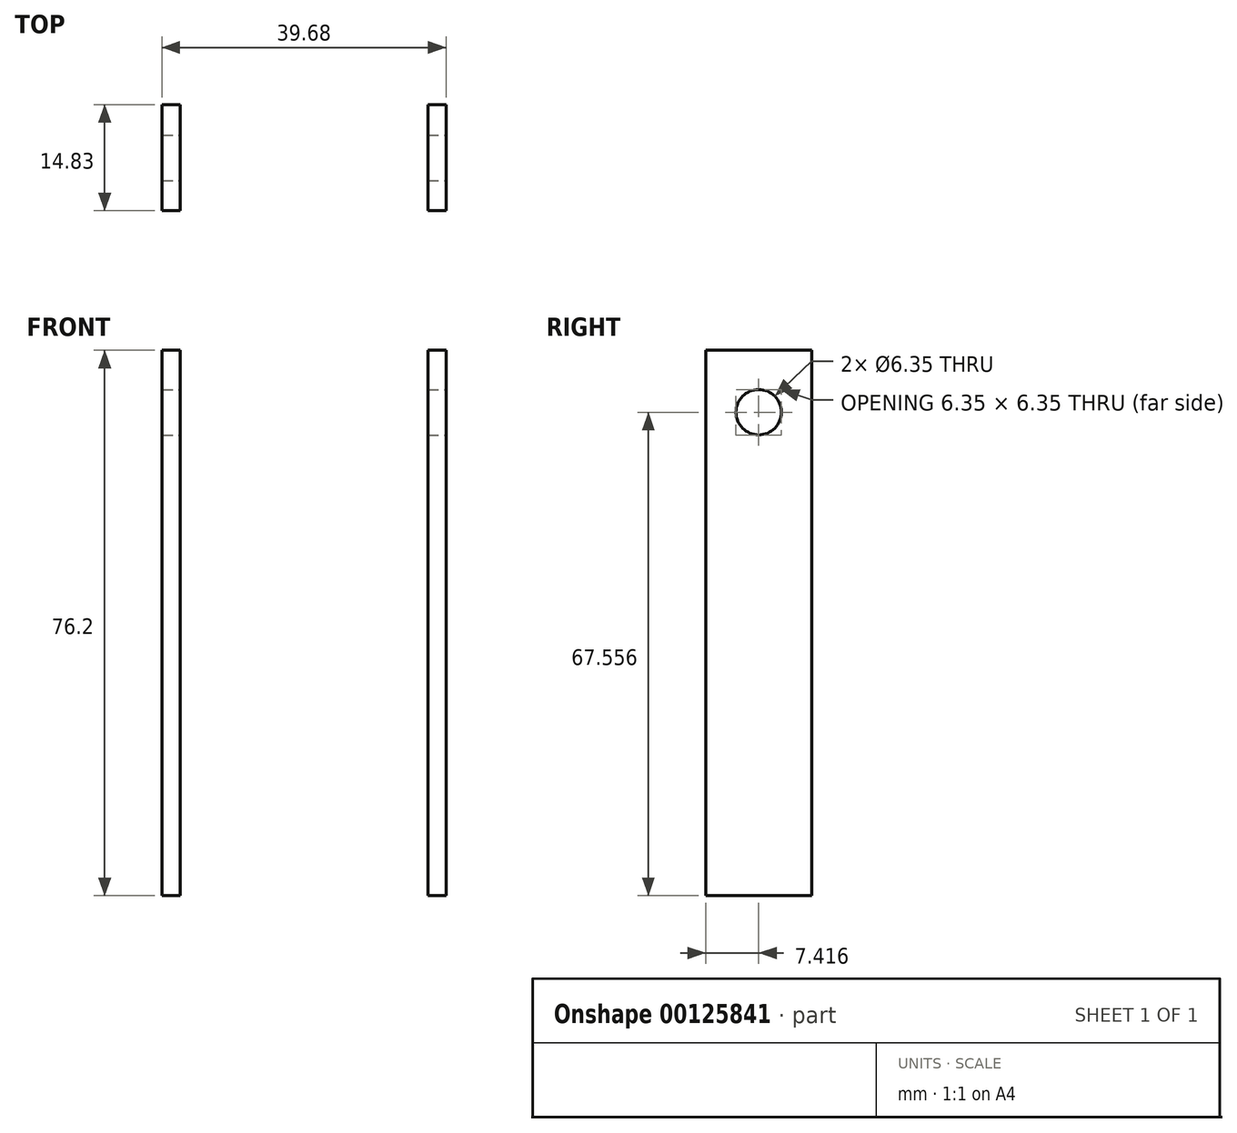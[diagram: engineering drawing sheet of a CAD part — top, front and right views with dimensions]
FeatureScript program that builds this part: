
annotation { "Feature Type Name" : "Feature", "Feature Type Description" : "" }
export const myFeature = defineFeature(function(context is Context, id is Id, definition is map)
    precondition{}
    {
        {
            var Q0;
            Q0=qCreatedBy(makeId("Front.planeOp"),FACE);
            var sketch = newSketch(context, id + "F0", { "sketchPlane" : qUnion([Q0])});
            skLineSegment(sketch, "E0", {"start": v(-12.93, -36.38) * mm, "end": v(-12.93, 39.82) * mm});
            skLineSegment(sketch, "E1", {"start": v(-12.93, 39.82) * mm, "end": v(-10.4, 39.82) * mm});
            skLineSegment(sketch, "E2", {"start": v(-10.4, 39.82) * mm, "end": v(-10.4, -36.38) * mm});
            skLineSegment(sketch, "E3", {"start": v(-10.4, -36.38) * mm, "end": v(-12.93, -36.38) * mm});
            skLineSegment(sketch, "E4", {"start": v(24.21, -36.38) * mm, "end": v(24.21, 39.82) * mm});
            skLineSegment(sketch, "E5", {"start": v(24.21, 39.82) * mm, "end": v(26.75, 39.82) * mm});
            skLineSegment(sketch, "E6", {"start": v(26.75, 39.82) * mm, "end": v(26.75, -36.38) * mm});
            skLineSegment(sketch, "E7", {"start": v(26.75, -36.38) * mm, "end": v(24.21, -36.38) * mm});
            skLineSegment(sketch, "E8", {"start": v(-10.4, 39.82) * mm, "end": v(24.21, 39.82) * mm, "construction": true});
            skSolve(sketch);
        }
        {
            var Q0;
            Q0 = qSketchRegion(id + "F0", true);
            extrude(context, id + "F1", {"entities" : qUnion([Q0]), "depth" : 14.83 * mm});
        }
        {
            var Q0;
            Q0=makeQuery(id+"F1.opExtrude","SWEPT_FACE",FACE,{"disambiguationData":[OSD([sQuery(id+"F0.wireOp",EDGE,"E6")])]});
            var sketch = newSketch(context, id + "F2", { "sketchPlane" : qUnion([Q0])});
            skCircle(sketch, "E9", {"center": v(-7.41, 31.18) * mm, "radius": 3.18 * mm});
            skPoint(sketch, "E9.centerSnap0", {"position": v(-7.41, 39.82) * mm});
            skSolve(sketch);
        }
        {
            var Q0;
            Q0 = qSketchRegion(id + "F2", true);
            extrude(context, id + "F3", {"entities" : qUnion([Q0]), "operationType" : NewBodyOperationType.REMOVE, "oppositeDirection" : true, "depth" : 50.97 * mm});
        }
    });
